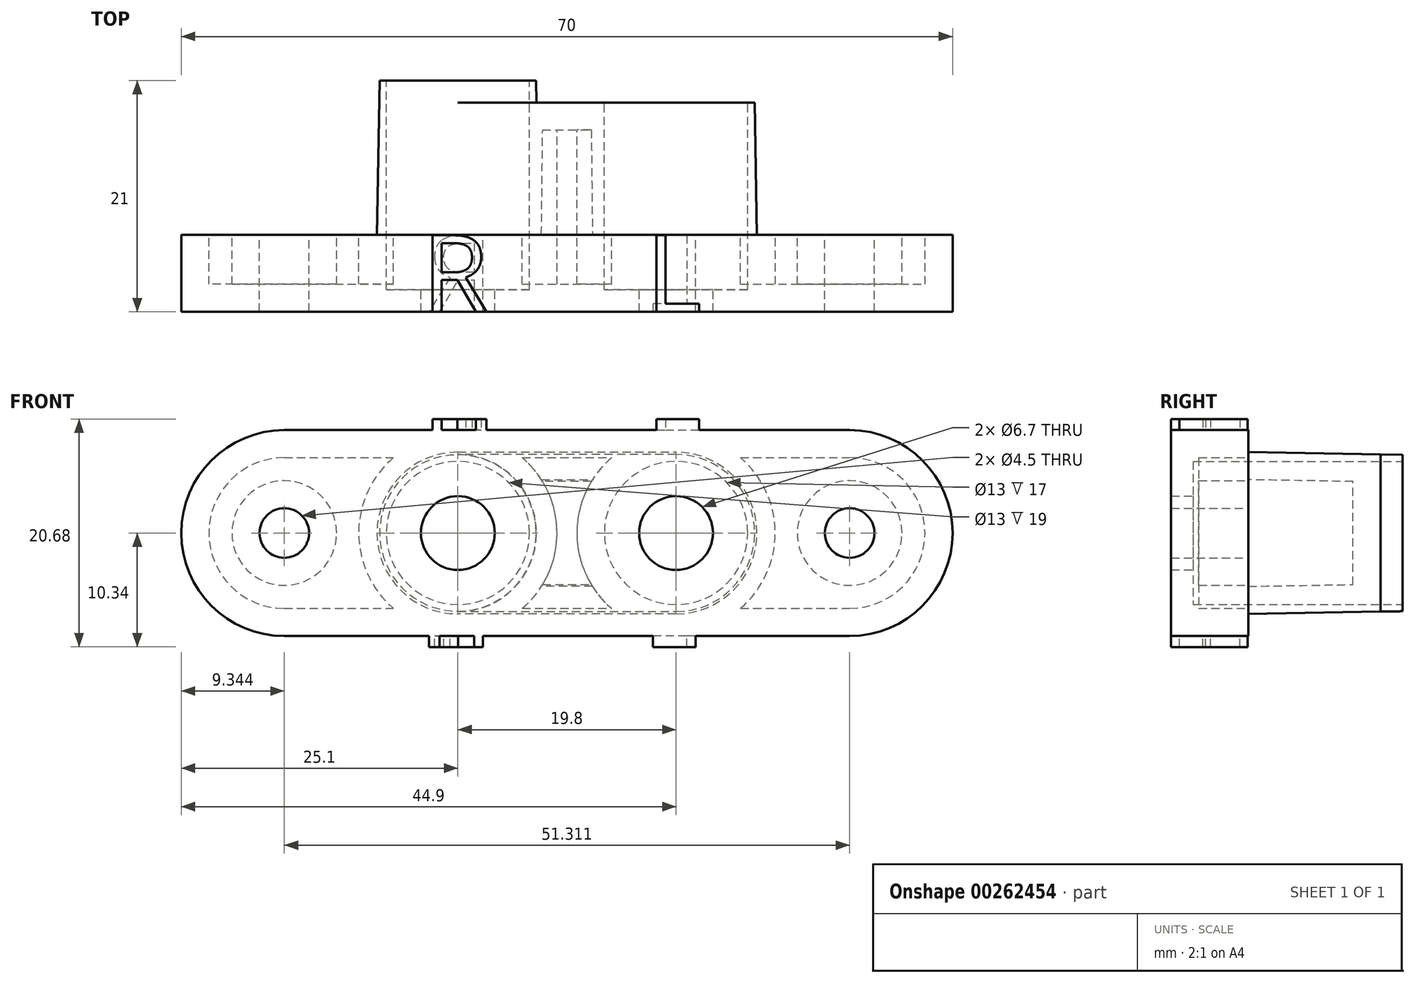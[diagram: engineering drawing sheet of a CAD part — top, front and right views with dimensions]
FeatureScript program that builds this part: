
annotation { "Feature Type Name" : "Feature", "Feature Type Description" : "" }
export const myFeature = defineFeature(function(context is Context, id is Id, definition is map)
    precondition{}
    {
        {
            var Q0;
            Q0=qCreatedBy(makeId("Front.planeOp"),FACE);
            var sketch = newSketch(context, id + "F0", { "sketchPlane" : qUnion([Q0])});
            skArc(sketch, "E0", {"start": v(-9.9, 7.1) * mm, "mid": v(-17, 0) * mm, "end": v(-9.9, -7.1) * mm});
            skArc(sketch, "E1", {"start": v(9.9, -7.1) * mm, "mid": v(17, 0) * mm, "end": v(9.9, 7.1) * mm});
            skLineSegment(sketch, "E2", {"start": v(-9.9, 0) * mm, "end": v(9.9, 0) * mm, "construction": true});
            skLineSegment(sketch, "E3", {"start": v(-9.9, 7.1) * mm, "end": v(9.9, 7.1) * mm});
            skLineSegment(sketch, "E4", {"start": v(-9.9, -7.1) * mm, "end": v(9.9, -7.1) * mm});
            skCircle(sketch, "E5", {"center": v(-9.9, 0) * mm, "radius": 6.5 * mm, "construction": true});
            skCircle(sketch, "E6", {"center": v(9.9, 0) * mm, "radius": 6.5 * mm, "construction": true});
            skSolve(sketch);
        }
        {
            var Q0;
            Q0 = qSketchRegion(id + "F0", true);
            extrude(context, id + "F1", {"entities" : qUnion([Q0]), "depth" : 14 * mm, "hasDraft" : true, "draftAngle" : 1 * degree});
        }
        {
            var Q0;
            Q0=makeQuery(id+"F1.opExtrude","CAP_FACE",FACE,{"disambiguationData":[OSD([sQuery(id+"F0.wireOp",EDGE,"E0"),sQuery(id+"F0.wireOp",EDGE,"E1"),sQuery(id+"F0.wireOp",EDGE,"E3"),sQuery(id+"F0.wireOp",EDGE,"E4"),sQuery(id+"F0.wireOp",EDGE,"E5"),sQuery(id+"F0.wireOp",EDGE,"E6")])],"isStart":false});
            var sketch = newSketch(context, id + "F2", { "sketchPlane" : qUnion([Q0])});
            skLineSegment(sketch, "E7.0", {"start": v(-25.66, 9.34) * mm, "end": v(25.66, 9.34) * mm});
            skArc(sketch, "E7.1", {"start": v(-25.66, 9.34) * mm, "mid": v(-35, 0) * mm, "end": v(-25.66, -9.34) * mm});
            skLineSegment(sketch, "E7.2", {"start": v(-25.66, -9.34) * mm, "end": v(25.66, -9.34) * mm});
            skArc(sketch, "E7.3", {"start": v(25.66, -9.34) * mm, "mid": v(35, 0) * mm, "end": v(25.66, 9.34) * mm});
            skLineSegment(sketch, "E8", {"start": v(-25.66, 0) * mm, "end": v(25.66, 0) * mm, "construction": true});
            skCircle(sketch, "E9", {"center": v(-25.66, 0) * mm, "radius": 2.25 * mm});
            skCircle(sketch, "E10", {"center": v(25.66, 0) * mm, "radius": 2.25 * mm});
            skCircle(sketch, "E11", {"center": v(-9.9, 0) * mm, "radius": 3.35 * mm});
            skCircle(sketch, "E12", {"center": v(9.9, 0) * mm, "radius": 3.35 * mm});
            skSolve(sketch);
        }
        {
            var Q0;
            Q0 = qSketchRegion(id + "F2", true);
            extrude(context, id + "F3", {"entities" : qUnion([Q0]), "operationType" : NewBodyOperationType.ADD, "depth" : 7 * mm});
        }
        {
            var Q0;
            Q0=makeQuery(id+"F1.opExtrude","CAP_FACE",FACE,{"disambiguationData":[OSD([sQuery(id+"F0.wireOp",EDGE,"E0"),sQuery(id+"F0.wireOp",EDGE,"E1"),sQuery(id+"F0.wireOp",EDGE,"E3"),sQuery(id+"F0.wireOp",EDGE,"E4")])],"isStart":true});
            var sketch = newSketch(context, id + "F4", { "sketchPlane" : qUnion([Q0])});
            skCircle(sketch, "E13.0", {"center": v(9.9, 0) * mm, "radius": 6.5 * mm});
            skCircle(sketch, "E13.1", {"center": v(-9.9, 0) * mm, "radius": 6.5 * mm});
            skSolve(sketch);
        }
        {
            var Q0;
            Q0 = qSketchRegion(id + "F4", true);
            extrude(context, id + "F5", {"entities" : qUnion([Q0]), "operationType" : NewBodyOperationType.REMOVE, "oppositeDirection" : true, "depth" : 19 * mm});
        }
        {
            var Q0;
            Q0=makeQuery(id+"F1.opExtrude","CAP_FACE",FACE,{"disambiguationData":[OSD([sQuery(id+"F0.wireOp",EDGE,"E0"),sQuery(id+"F0.wireOp",EDGE,"E1"),sQuery(id+"F0.wireOp",EDGE,"E3"),sQuery(id+"F0.wireOp",EDGE,"E4"),sQuery(id+"F0.wireOp",EDGE,"E5"),sQuery(id+"F0.wireOp",EDGE,"E6")])],"isStart":true});
            var sketch = newSketch(context, id + "F6", { "sketchPlane" : qUnion([Q0])});
            skArc(sketch, "E14", {"start": v(9.9, 7.1) * mm, "mid": v(2.8, 0) * mm, "end": v(9.9, -7.1) * mm});
            skLineSegment(sketch, "E15.0", {"start": v(9.9, 7.1) * mm, "end": v(-9.9, 7.1) * mm, "construction": true});
            skArc(sketch, "E16.0", {"start": v(-9.9, -7.1) * mm, "mid": v(-17, 0) * mm, "end": v(-9.9, 7.1) * mm, "construction": true});
            skLineSegment(sketch, "E17.0", {"start": v(9.9, -7.1) * mm, "end": v(-9.9, -7.1) * mm, "construction": true});
            skLineSegment(sketch, "E18.0", {"start": v(13.09, -12.1) * mm, "end": v(-9.9, -12.1) * mm});
            skArc(sketch, "E18.1", {"start": v(-9.9, -12.1) * mm, "mid": v(-22, 0) * mm, "end": v(-9.9, 12.1) * mm});
            skLineSegment(sketch, "E18.2", {"start": v(13.09, 12.1) * mm, "end": v(-9.9, 12.1) * mm});
            skLineSegment(sketch, "E19", {"start": v(13.09, -7.1) * mm, "end": v(13.09, -12.1) * mm});
            skLineSegment(sketch, "E20", {"start": v(13.09, 12.1) * mm, "end": v(13.09, 7.1) * mm});
            skLineSegment(sketch, "E21", {"start": v(9.9, 7.1) * mm, "end": v(13.09, 7.1) * mm});
            skLineSegment(sketch, "E22", {"start": v(9.9, -7.1) * mm, "end": v(13.09, -7.1) * mm});
            skSolve(sketch);
        }
        {
            var Q0;
            Q0 = qSketchRegion(id + "F6", true);
            extrude(context, id + "F7", {"entities" : qUnion([Q0]), "operationType" : NewBodyOperationType.REMOVE, "oppositeDirection" : true, "depth" : 2 * mm, "hasDraft" : true, "draftAngle" : 1 * degree, "draftPullDirection" : true});
        }
        {
            var Q0;
            Q0=makeQuery(id+"F3.opExtrude","CAP_FACE",FACE,{"disambiguationData":[OSD([sQuery(id+"F2.wireOp",EDGE,"E7.0"),sQuery(id+"F2.wireOp",EDGE,"E7.1"),sQuery(id+"F2.wireOp",EDGE,"E7.2"),sQuery(id+"F2.wireOp",EDGE,"E7.3"),sQuery(id+"F2.wireOp",EDGE,"E9"),sQuery(id+"F2.wireOp",EDGE,"E10"),sQuery(id+"F2.wireOp",EDGE,"E11"),sQuery(id+"F2.wireOp",EDGE,"E12")])],"isStart":true});
            shell(context, id + "F8", {"entities" : qUnion([Q0]), "thickness" : 2.5 * mm});
        }
        {
            var Q0;
            Q0=makeQuery(id+"F3.opExtrude","SWEPT_FACE",FACE,{"disambiguationData":[OSD([sQuery(id+"F2.wireOp",EDGE,"E7.2")])]});
            var sketch = newSketch(context, id + "F9", { "sketchPlane" : qUnion([Q0])});
            skText(sketch, "E23", { "text": "L", "fontName": "OpenSans-Regular.ttf"});
            skLineSegment(sketch, "E24", {"start": v(9.9, 14) * mm, "end": v(9.9, 21) * mm, "construction": true});
            skLineSegment(sketch, "E25", {"start": v(-9.9, 14) * mm, "end": v(-9.9, 21) * mm, "construction": true});
            skText(sketch, "E26", { "text": "R", "fontName": "OpenSans-Regular.ttf"});
            const initialGuessF9  = {"E23": [0.01263, 0.021, -1, 0, 0.007], "E26": [-0.00666, 0.021, -1, 0, 0.007]};
            skSetInitialGuess(sketch, initialGuessF9);
            skSolve(sketch);
        }
        {
            var Q0;
            Q0 = qSketchRegion(id + "F9", true);
            extrude(context, id + "F10", {"entities" : qUnion([Q0]), "operationType" : NewBodyOperationType.ADD, "depth" : 1 * mm});
        }
        {
            var Q0;
            Q0=makeQuery(id+"F3.opExtrude","SWEPT_FACE",FACE,{"disambiguationData":[OSD([sQuery(id+"F2.wireOp",EDGE,"E7.0")])]});
            var sketch = newSketch(context, id + "F11", { "sketchPlane" : qUnion([Q0])});
            skLineSegment(sketch, "E27", {"start": v(-9.9, -14) * mm, "end": v(-9.9, -21) * mm, "construction": true});
            skLineSegment(sketch, "E28", {"start": v(9.9, -14) * mm, "end": v(9.9, -21) * mm, "construction": true});
            skText(sketch, "E29", { "text": "L", "fontName": "OpenSans-Regular.ttf"});
            skText(sketch, "E30", { "text": "R", "fontName": "OpenSans-Regular.ttf"});
            const initialGuessF11  = {"E29": [0.00717, -0.021, 1, 0, 0.007], "E30": [-0.01314, -0.021, 1, 0, 0.007]};
            skSetInitialGuess(sketch, initialGuessF11);
            skSolve(sketch);
        }
        {
            var Q0;
            Q0 = qSketchRegion(id + "F11", true);
            extrude(context, id + "F12", {"entities" : qUnion([Q0]), "operationType" : NewBodyOperationType.ADD, "depth" : 1 * mm});
        }
    });
